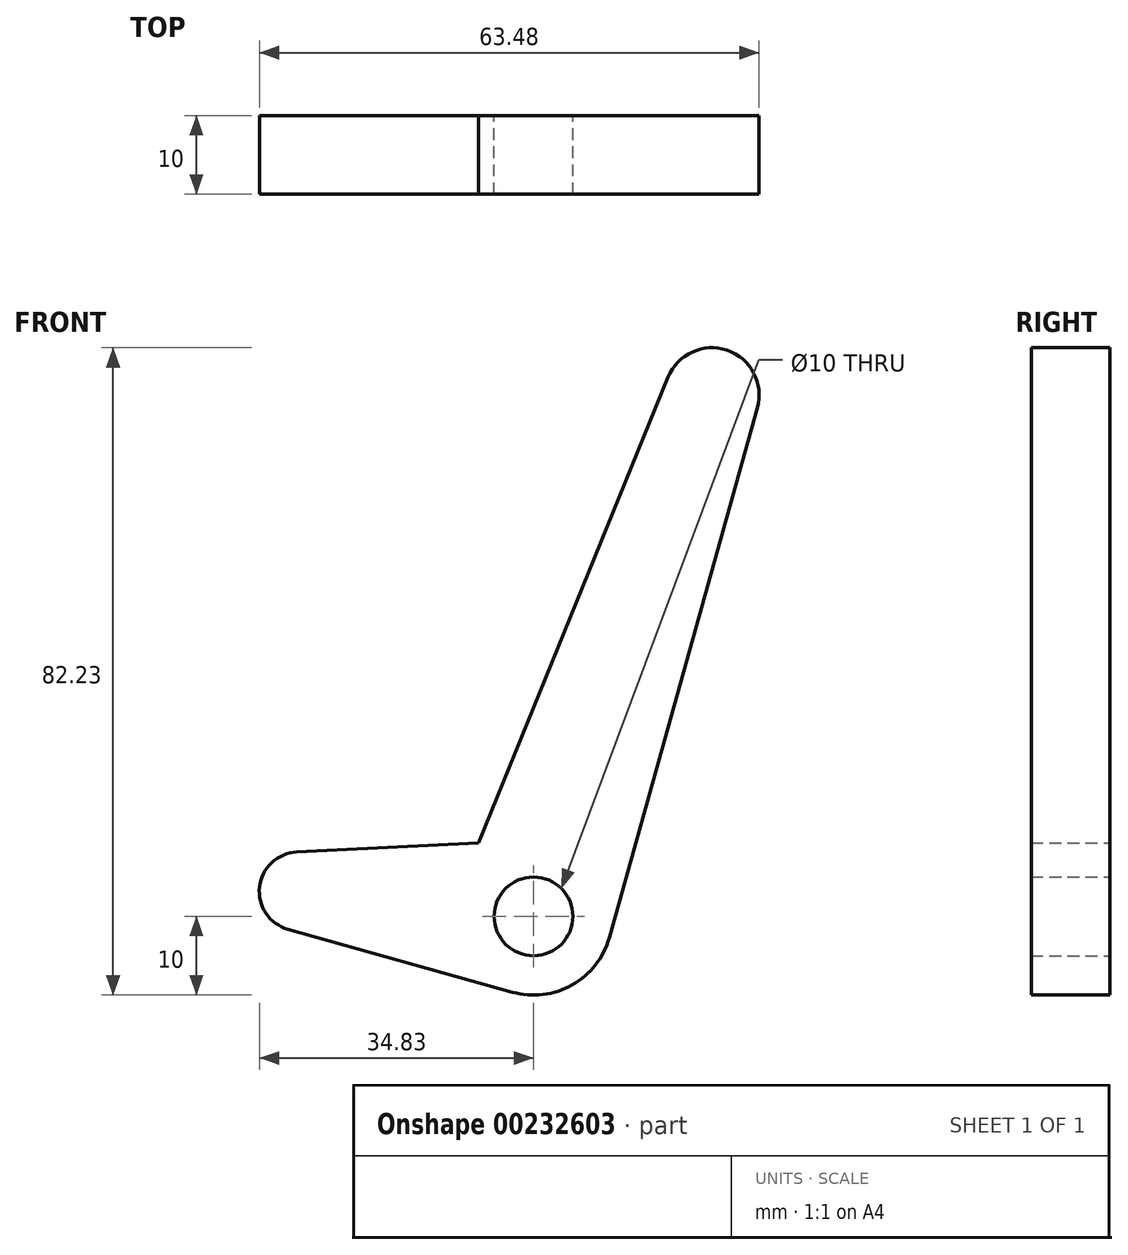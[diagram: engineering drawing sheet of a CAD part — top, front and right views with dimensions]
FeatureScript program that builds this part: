
annotation { "Feature Type Name" : "Feature", "Feature Type Description" : "" }
export const myFeature = defineFeature(function(context is Context, id is Id, definition is map)
    precondition{}
    {
        {
            var Q0;
            Q0=qCreatedBy(makeId("Front.planeOp"),FACE);
            var sketch = newSketch(context, id + "F0", { "sketchPlane" : qUnion([Q0])});
            skCircle(sketch, "E0", {"center": v(0, 0) * mm, "radius": 5 * mm});
            skArc(sketch, "E1", {"start": v(-2.7, -9.63) * mm, "mid": v(4.9, -8.71) * mm, "end": v(9.63, -2.69) * mm});
            skArc(sketch, "E2", {"start": v(28.43, 64.62) * mm, "mid": v(24.6, 71.91) * mm, "end": v(17.1, 68.5) * mm});
            skLineSegment(sketch, "E3", {"start": v(17.1, 68.5) * mm, "end": v(-7, 9.35) * mm});
            skLineSegment(sketch, "E4", {"start": v(28.43, 64.62) * mm, "end": v(9.63, -2.69) * mm});
            skArc(sketch, "E5", {"start": v(-30.09, 8.16) * mm, "mid": v(-34.8, 3.72) * mm, "end": v(-31.18, -1.65) * mm});
            skLineSegment(sketch, "E6", {"start": v(-30.09, 8.16) * mm, "end": v(-7, 9.35) * mm});
            skLineSegment(sketch, "E7", {"start": v(-31.18, -1.65) * mm, "end": v(-2.7, -9.63) * mm});
            skSolve(sketch);
        }
        {
            var Q0;
            Q0 = qSketchRegion(id + "F0", true);
            extrude(context, id + "F1", {"entities" : qUnion([Q0]), "depth" : 10 * mm});
        }
    });
